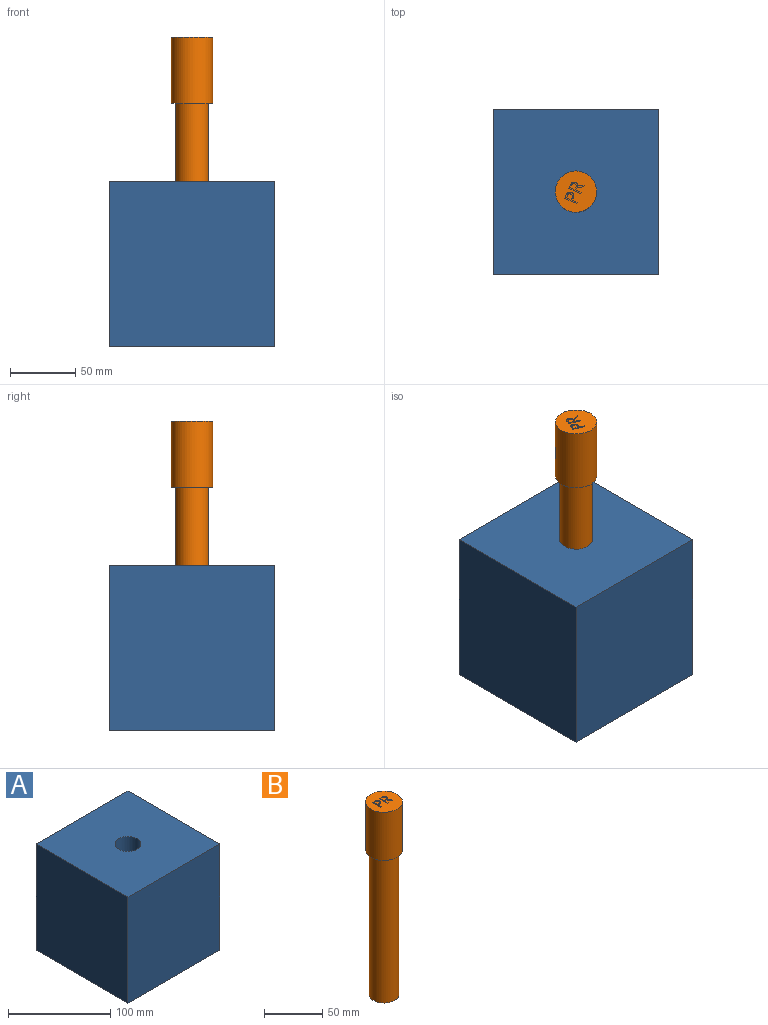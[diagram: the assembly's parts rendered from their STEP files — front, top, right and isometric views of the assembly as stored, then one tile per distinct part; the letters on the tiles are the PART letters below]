
ASSEMBLY  parts=2 mates=1
PART A: 7 faces, bbox 127x127x127 mm
  f0: plane 127x127mm, normal (0,-1,0), area 16129mm2, adj f1,f4,f5,f6
  f1: plane 127x127mm, normal (1,0,0), area 16129mm2, adj f0,f2,f5,f6
  f2: plane 127x127mm, normal (0,1,0), area 16129mm2, adj f1,f4,f5,f6
  f3: cylinder r=12.7mm len=127mm, axis (0,0,-1), area 10134.1mm2, adj f5,f6
  f4: plane 127x127mm, normal (-1,0,0), area 16129mm2, adj f0,f2,f5,f6
  f5: plane 127x127mm, normal (0,0,1), area 15622.3mm2, adj f0,f1,f2,f3,f4
  f6: plane 127x127mm, normal (0,0,-1), area 15622.3mm2, adj f0,f1,f2,f3,f4
PART B: 42 faces, bbox 31.8x31.8x203.2 mm
  f0: plane 31.75x31.75mm, normal (0,0,1), area 711.3mm2, adj f3,f11,f12,f13,f14,f15,f16,f17
  f1: cylinder r=12.7mm len=152.4mm, axis (0,0,-1), area 12161mm2, adj f2,f4
  f2: plane 25.4x25.4mm, normal (0,0,-1), area 506.7mm2, adj f1
  f3: cylinder r=15.88mm len=50.8mm, axis (0,0,-1), area 5067.1mm2, adj f0,f4
  f4: plane 31.75x31.75mm, normal (0,0,-1), area 285mm2, adj f1,f3
  f5: plane 3.18x1.57mm, normal (0,-1,0), area 5mm2, adj f6,f22,f23,f40
  f6: plane 3.77x3.18mm, normal (-1,0,0), area 12mm2, adj f5,f7,f23,f40
  f7: plane 3.18x1.49mm, normal (0,1,0), area 4.7mm2, adj f6,f8,f23,f40
  f8: extruded ~3.18x1.85mm, area 6.1mm2, adj f7,f9,f23,f40
  f9: extruded ~3.18x1.41mm, area 5mm2, adj f8,f10,f23,f40
  f10: extruded ~3.18x1.45mm, area 5.1mm2, adj f9,f22,f23,f40
  f11: plane 4.1x3.18mm, normal (-1,0,0), area 13mm2, adj f0,f12,f21,f23
  f12: plane 3.18x2.06mm, normal (0,1,0), area 6.5mm2, adj f0,f11,f13,f23
  f13: plane 4.1x3.18mm, normal (0.86,0.5,0), area 15.1mm2, adj f0,f12,f14,f23
  f14: plane 3.18x1.36mm, normal (0,1,0), area 4.3mm2, adj f0,f13,f15,f23
  f15: plane 4.43x3.18mm, normal (-0.86,-0.52,0), area 16.4mm2, adj f0,f14,f16,f23
  f16: extruded ~3.18x2.64mm, area 11.3mm2, adj f0,f15,f17,f23
  f17: extruded ~3.18x2.09mm, area 7.4mm2, adj f0,f16,f18,f23
  f18: extruded ~3.18x2.68mm, area 9mm2, adj f0,f17,f19,f23
  f19: plane 3.18x2.7mm, normal (0,-1,0), area 8.6mm2, adj f0,f18,f20,f23
  f20: plane 9.86x3.18mm, normal (1,0,0), area 31.3mm2, adj f0,f19,f21,f23
  f21: plane 3.18x1.15mm, normal (0,1,0), area 3.6mm2, adj f0,f11,f20,f23
  f22: extruded ~3.18x1.78mm, area 6mm2, adj f5,f10,f23,f40
  f23: plane 9.86x6.95mm, normal (0,0,1), area 29.2mm2, adj f5,f6,f7,f8,f9,f10,f11,f12
  f24: plane 3.18x1.03mm, normal (0,-1,0), area 3.3mm2, adj f25,f38,f39,f41
  f25: plane 4.01x3.18mm, normal (-1,0,0), area 12.7mm2, adj f24,f26,f39,f41
  f26: plane 3.18x1.28mm, normal (0,1,0), area 4.1mm2, adj f25,f27,f39,f41
  f27: extruded ~3.18x2mm, area 6.6mm2, adj f26,f28,f39,f41
  f28: extruded ~3.18x1.46mm, area 5.3mm2, adj f27,f29,f39,f41
  f29: extruded ~3.18x1.58mm, area 5.7mm2, adj f28,f38,f39,f41
  f30: extruded ~3.18x2.3mm, area 8.3mm2, adj f0,f31,f37,f39
  f31: extruded ~3.69x3.18mm, area 17mm2, adj f0,f30,f32,f39
  f32: plane 3.18x2.56mm, normal (0,-1,0), area 8.1mm2, adj f0,f31,f33,f39
  f33: plane 9.86x3.18mm, normal (1,0,0), area 31.3mm2, adj f0,f32,f34,f39
  f34: plane 3.18x1.15mm, normal (0,1,0), area 3.6mm2, adj f0,f33,f35,f39
  f35: plane 3.88x3.18mm, normal (-1,0,0), area 12.3mm2, adj f0,f34,f36,f39
  f36: plane 3.18x1.16mm, normal (0,1,0), area 3.7mm2, adj f0,f35,f37,f39
  f37: extruded ~3.18x2.92mm, area 9.8mm2, adj f0,f30,f36,f39
  f38: extruded ~3.18x2.2mm, area 7.3mm2, adj f24,f29,f39,f41
  f39: plane 9.86x6.25mm, normal (0,0,1), area 24mm2, adj f24,f25,f26,f27,f28,f29,f30,f31
  f40: plane 3.92x3.77mm, normal (0,0,1), area 13.4mm2, adj f5,f6,f7,f8,f9,f10,f22
  f41: plane 4.01x3.92mm, normal (0,0,1), area 14mm2, adj f24,f25,f26,f27,f28,f29,f38
PLACE A at identity
PLACE B rot(axis=(0,0,1),67.5deg) t=(0,0,34.53)mm
MATE cylindrical A.f3 <-> B.f1  axis (0,0,1) through (0,0,127)mm
